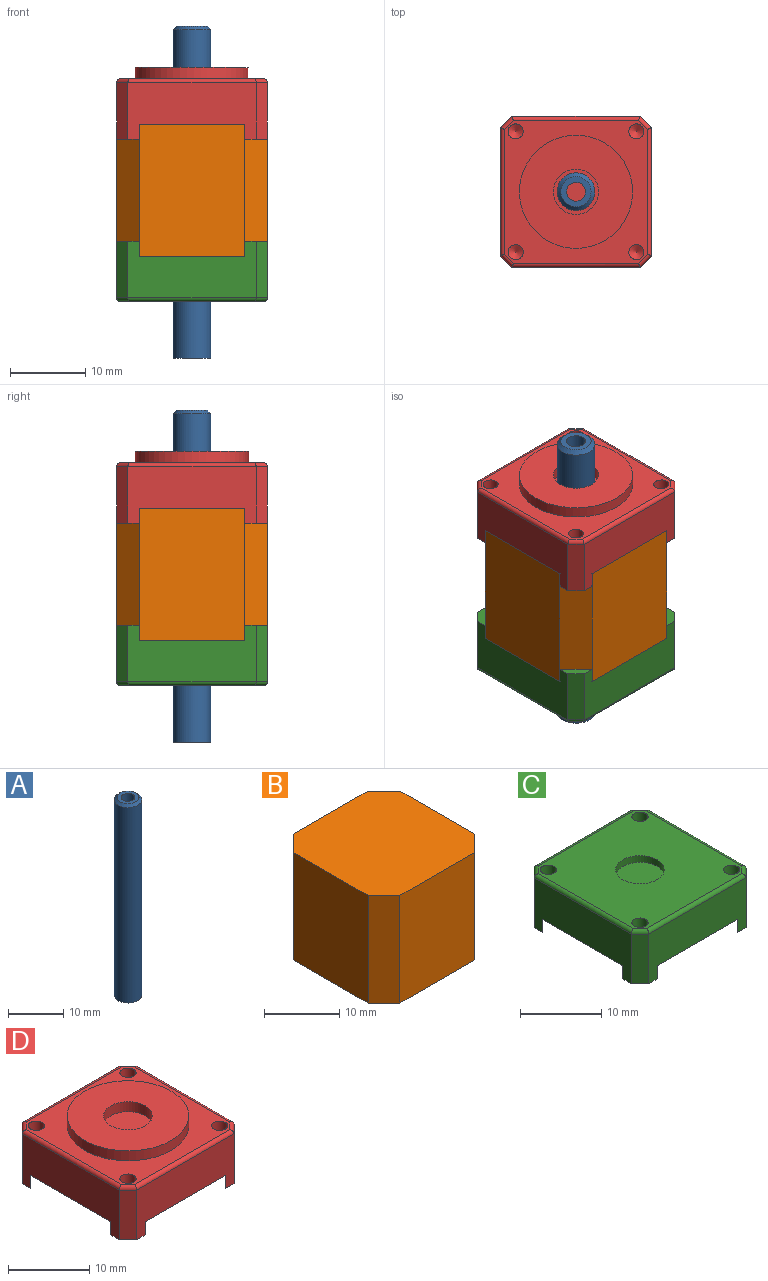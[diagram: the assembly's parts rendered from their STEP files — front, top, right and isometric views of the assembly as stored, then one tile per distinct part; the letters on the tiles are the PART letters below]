
ASSEMBLY  parts=4 mates=3
PART A: 5 faces, bbox 5x5x44 mm
  f0: cylinder r=2.5mm len=43.5mm, axis (0,0,-1), area 683.3mm2, adj f2,f3
  f1: plane 4x4mm, normal (0,0,1), area 7.7mm2, adj f2,f4
  f2: cone r=2mm half-angle=45deg, axis (0,0,-1), area 10mm2, adj f0,f1
  f3: plane 5x5mm, normal (0,0,-1), area 14.7mm2, adj f0,f4
  f4: cylinder r=1.25mm len=44mm, axis (0,0,1), area 345.6mm2, adj f1,f3
PART B: 10 faces, bbox 20x20x17.5 mm
  f0: plane 17.5x14mm, normal (0,1,0), area 245mm2, adj f1,f7,f8,f9
  f1: plane 17.5x3mm, normal (-0.71,0.71,0), area 74.2mm2, adj f0,f2,f8,f9
  f2: plane 17.5x14mm, normal (-1,0,0), area 245mm2, adj f1,f3,f8,f9
  f3: plane 17.5x3mm, normal (-0.71,-0.71,0), area 74.2mm2, adj f2,f4,f8,f9
  f4: plane 17.5x14mm, normal (0,-1,0), area 245mm2, adj f3,f5,f8,f9
  f5: plane 17.5x3mm, normal (0.71,-0.71,0), area 74.2mm2, adj f4,f6,f8,f9
  f6: plane 17.5x14mm, normal (1,0,0), area 245mm2, adj f5,f7,f8,f9
  f7: plane 17.5x3mm, normal (0.71,0.71,0), area 74.2mm2, adj f0,f6,f8,f9
  f8: plane 20x20mm, normal (0,0,1), area 382mm2, adj f0,f1,f2,f3,f4,f5,f6,f7
  f9: plane 20x20mm, normal (0,0,-1), area 382mm2, adj f0,f1,f2,f3,f4,f5,f6,f7
PART C: 36 faces, bbox 20x20x8 mm
  f0: plane 20x20mm, normal (0,0,-1), area 382mm2, adj f1,f3,f5,f7,f12,f14,f16,f18
  f1: plane 17x7.5mm, normal (0,1,0), area 99.5mm2, adj f0,f2,f8,f14,f15,f18,f19,f30
  f2: plane 7.5x1.5mm, normal (-0.71,0.71,0), area 15.9mm2, adj f1,f3,f19,f32
  f3: plane 17x7.5mm, normal (-1,0,0), area 99.5mm2, adj f0,f2,f4,f16,f17,f18,f19,f34
  f4: plane 7.5x1.5mm, normal (-0.71,-0.71,0), area 15.9mm2, adj f3,f5,f17,f35
  f5: plane 17x7.5mm, normal (0,-1,0), area 99.5mm2, adj f0,f4,f6,f12,f13,f16,f17,f33
  f6: plane 7.5x1.5mm, normal (0.71,-0.71,0), area 15.9mm2, adj f5,f7,f13,f31
  f7: plane 17x7.5mm, normal (1,0,0), area 99.5mm2, adj f0,f6,f8,f12,f13,f14,f15,f29
  f8: plane 7.5x1.5mm, normal (0.71,0.71,0), area 15.9mm2, adj f1,f7,f15,f28
  f9: plane 19x19mm, normal (0,0,1), area 317.2mm2, adj f10,f21,f23,f25,f27,f28,f29,f30
  f10: cylinder r=3mm len=6mm, axis (0,0,1), area 18.8mm2, adj f9,f11
  f11: plane 6x6mm, normal (0,0,1), area 28.3mm2, adj f10
  f12: plane 3x3mm, normal (-0.71,0.71,0), area 8.5mm2, adj f0,f5,f7,f13
  f13: plane 3x3mm, normal (0,0,-1), area 3.4mm2, adj f5,f6,f7,f12
  f14: plane 3x3mm, normal (-0.71,-0.71,0), area 8.5mm2, adj f0,f1,f7,f15
  f15: plane 3x3mm, normal (0,0,-1), area 3.4mm2, adj f1,f7,f8,f14
  f16: plane 3x3mm, normal (0.71,0.71,0), area 8.5mm2, adj f0,f3,f5,f17
  f17: plane 3x3mm, normal (0,0,-1), area 3.4mm2, adj f3,f4,f5,f16
  f18: plane 3x3mm, normal (0.71,-0.71,0), area 8.5mm2, adj f0,f1,f3,f19
  f19: plane 3x3mm, normal (0,0,-1), area 3.4mm2, adj f1,f2,f3,f18
  f20: cone r=0mm half-angle=59deg, axis (0,0,1), area 3.7mm2, adj f21
  f21: cylinder r=1mm len=3mm, axis (0,0,1), area 18.8mm2, adj f9,f20
  f22: cone r=0mm half-angle=59deg, axis (0,0,1), area 3.7mm2, adj f23
  f23: cylinder r=1mm len=3mm, axis (0,0,1), area 18.8mm2, adj f9,f22
  f24: cone r=0mm half-angle=59deg, axis (0,0,1), area 3.7mm2, adj f25
  f25: cylinder r=1mm len=3mm, axis (0,0,1), area 18.8mm2, adj f9,f24
  f26: cone r=0mm half-angle=59deg, axis (0,0,1), area 3.7mm2, adj f27
  f27: cylinder r=1mm len=3mm, axis (0,0,1), area 18.8mm2, adj f9,f26
  f28: cylinder r=0.5mm len=1.85mm, axis (-0.71,0.71,0), area 1.5mm2, adj f8,f9,f29,f30
  f29: cylinder r=0.5mm len=17mm, axis (0,1,0), area 13.2mm2, adj f7,f9,f28,f31
  f30: cylinder r=0.5mm len=17mm, axis (-1,0,0), area 13.2mm2, adj f1,f9,f28,f32
  f31: cylinder r=0.5mm len=1.85mm, axis (0.71,0.71,0), area 1.5mm2, adj f6,f9,f29,f33
  f32: cylinder r=0.5mm len=1.85mm, axis (-0.71,-0.71,0), area 1.5mm2, adj f2,f9,f30,f34
  f33: cylinder r=0.5mm len=17mm, axis (1,0,0), area 13.2mm2, adj f5,f9,f31,f35
  f34: cylinder r=0.5mm len=17mm, axis (0,-1,0), area 13.2mm2, adj f3,f9,f32,f35
  f35: cylinder r=0.5mm len=1.85mm, axis (0.71,-0.71,0), area 1.5mm2, adj f4,f9,f33,f34
PART D: 38 faces, bbox 20x20x9.5 mm
  f0: plane 20x20mm, normal (0,0,-1), area 382mm2, adj f1,f3,f5,f7,f14,f16,f18,f20
  f1: plane 17x7.5mm, normal (0,-1,0), area 99.5mm2, adj f0,f2,f8,f16,f17,f20,f21,f37
  f2: plane 7.5x1.5mm, normal (0.71,-0.71,0), area 15.9mm2, adj f1,f3,f17,f35
  f3: plane 17x7.5mm, normal (1,0,0), area 99.5mm2, adj f0,f2,f4,f14,f15,f16,f17,f33
  f4: plane 7.5x1.5mm, normal (0.71,0.71,0), area 15.9mm2, adj f3,f5,f15,f31
  f5: plane 17x7.5mm, normal (0,1,0), area 99.5mm2, adj f0,f4,f6,f14,f15,f18,f19,f30
  f6: plane 7.5x1.5mm, normal (-0.71,0.71,0), area 15.9mm2, adj f5,f7,f19,f32
  f7: plane 17x7.5mm, normal (-1,0,0), area 99.5mm2, adj f0,f6,f8,f18,f19,f20,f21,f34
  f8: plane 7.5x1.5mm, normal (-0.71,-0.71,0), area 15.9mm2, adj f1,f7,f21,f36
  f9: plane 19x19mm, normal (0,0,1), area 168.8mm2, adj f11,f23,f25,f27,f29,f30,f31,f32
  f10: cylinder r=3mm len=6mm, axis (0,0,-1), area 28.3mm2, adj f12,f13
  f11: cylinder r=7.5mm len=15mm, axis (0,0,-1), area 70.7mm2, adj f9,f12
  f12: plane 15x15mm, normal (0,0,1), area 148.4mm2, adj f10,f11
  f13: plane 6x6mm, normal (0,0,1), area 28.3mm2, adj f10
  f14: plane 3x3mm, normal (-0.71,-0.71,0), area 8.5mm2, adj f0,f3,f5,f15
  f15: plane 3x3mm, normal (0,0,-1), area 3.4mm2, adj f3,f4,f5,f14
  f16: plane 3x3mm, normal (-0.71,0.71,0), area 8.5mm2, adj f0,f1,f3,f17
  f17: plane 3x3mm, normal (0,0,-1), area 3.4mm2, adj f1,f2,f3,f16
  f18: plane 3x3mm, normal (0.71,-0.71,0), area 8.5mm2, adj f0,f5,f7,f19
  f19: plane 3x3mm, normal (0,0,-1), area 3.4mm2, adj f5,f6,f7,f18
  f20: plane 3x3mm, normal (0.71,0.71,0), area 8.5mm2, adj f0,f1,f7,f21
  f21: plane 3x3mm, normal (0,0,-1), area 3.4mm2, adj f1,f7,f8,f20
  f22: cone r=0mm half-angle=59deg, axis (0,0,1), area 3.7mm2, adj f23
  f23: cylinder r=1mm len=3mm, axis (0,0,1), area 18.8mm2, adj f9,f22
  f24: cone r=0mm half-angle=59deg, axis (0,0,1), area 3.7mm2, adj f25
  f25: cylinder r=1mm len=3mm, axis (0,0,1), area 18.8mm2, adj f9,f24
  f26: cone r=0mm half-angle=59deg, axis (0,0,1), area 3.7mm2, adj f27
  f27: cylinder r=1mm len=3mm, axis (0,0,1), area 18.8mm2, adj f9,f26
  f28: cone r=0mm half-angle=59deg, axis (0,0,1), area 3.7mm2, adj f29
  f29: cylinder r=1mm len=3mm, axis (0,0,1), area 18.8mm2, adj f9,f28
  f30: cylinder r=0.5mm len=17mm, axis (-1,0,0), area 13.2mm2, adj f5,f9,f31,f32
  f31: cylinder r=0.5mm len=1.85mm, axis (-0.71,0.71,0), area 1.5mm2, adj f4,f9,f30,f33
  f32: cylinder r=0.5mm len=1.85mm, axis (-0.71,-0.71,0), area 1.5mm2, adj f6,f9,f30,f34
  f33: cylinder r=0.5mm len=17mm, axis (0,1,0), area 13.2mm2, adj f3,f9,f31,f35
  f34: cylinder r=0.5mm len=17mm, axis (0,-1,0), area 13.2mm2, adj f7,f9,f32,f36
  f35: cylinder r=0.5mm len=1.85mm, axis (0.71,0.71,0), area 1.5mm2, adj f2,f9,f33,f37
  f36: cylinder r=0.5mm len=1.85mm, axis (0.71,-0.71,0), area 1.5mm2, adj f8,f9,f34,f37
  f37: cylinder r=0.5mm len=17mm, axis (1,0,0), area 13.2mm2, adj f1,f9,f35,f36
PLACE A t=(-74.9,40,-7.76)mm
PLACE B rot(axis=(0,0,1),180deg) t=(-9.9,0,-31.26)mm
PLACE C rot(axis=(0,-1,0),180deg) t=(-99.9,0,-37.26)mm
PLACE D rot(axis=(0,0,1),180deg) t=(-49.9,0,-7.76)mm
MATE fastened B.f9 <-> C.f10  axis (0,0,-1) through (-49.9,0,-31.26)mm
MATE revolute A.f0 <-> D.f10  axis (0,0,-1) through (-49.9,0,-7.76)mm
MATE fastened B.f8 <-> D.f10  axis (0,0,1) through (-49.9,0,-13.76)mm
